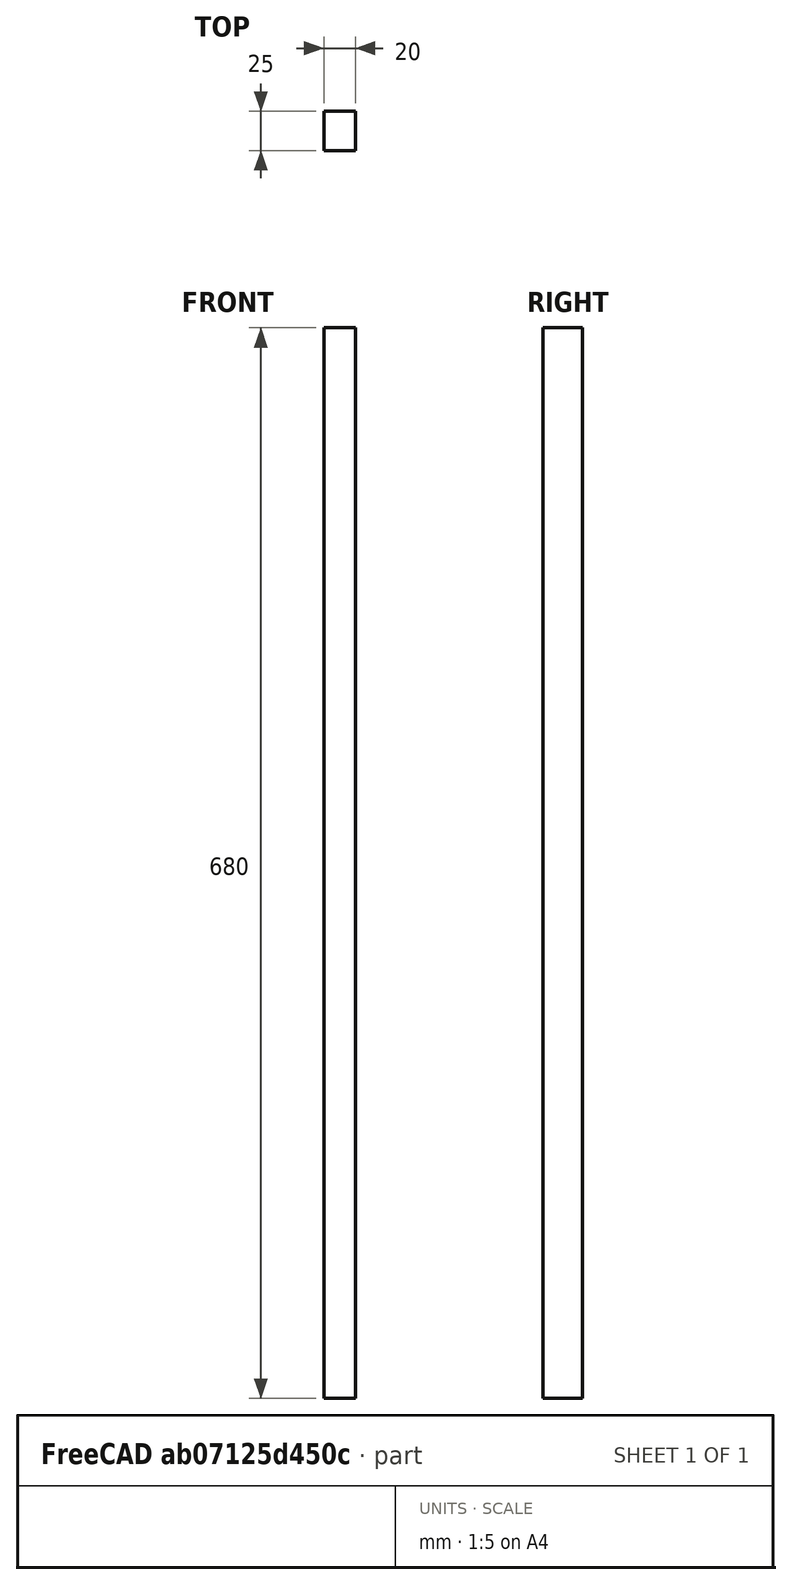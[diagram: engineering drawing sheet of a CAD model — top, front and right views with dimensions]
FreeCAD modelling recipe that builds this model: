
FCSTD DOCUMENT  (FreeCAD 0.21R33771 (Git))
Label: left_bed_rail
License: All rights reserved
LicenseURL: http://en.wikipedia.org/wiki/All_rights_reserved
objects: Sketcher::SketchObject×1, PartDesign::Pad×1, PartDesign::Body×1
note: 4 computed .brp shape members not serialized (recipe doc carries the construction recipe); baked Part::Feature solids carry a one-line shape summary decoded from their .brp

FEATURE [Sketcher::SketchObject] Sketch
  FullyConstrained = true
  MapMode = 5
  Support = -> [XY_Plane]
  sketch-geometry (4):
    g0: LineSegment StartX=-145 StartY=85 StartZ=0 EndX=-125 EndY=85 EndZ=0
    g1: LineSegment StartX=-125 StartY=85 StartZ=0 EndX=-125 EndY=60 EndZ=0
    g2: LineSegment StartX=-125 StartY=60 StartZ=0 EndX=-145 EndY=60 EndZ=0
    g3: LineSegment StartX=-145 StartY=60 StartZ=0 EndX=-145 EndY=85 EndZ=0
  constraints (12):
    c: Coincident(g0,g1)
    c: Coincident(g1,g2)
    c: Coincident(g2,g3)
    c: Coincident(g3,g0)
    c: Horizontal(g0)
    c: Horizontal(g2)
    c: Vertical(g1)
    c: Vertical(g3)
    c: DistanceX(g2,g2) = 20
    c: Distance(g1,g-2) = 125
    c: Distance(g1,g-1) = 60
    c: Distance(g2,g0) = 25
FEATURE [PartDesign::Pad] Pad001
  Direction = (0,0,1)
  Length = 680
  Length2 = 10
  Profile = -> Sketch
  ReferenceAxis = -> Sketch [N_Axis]
  Type = 0
FEATURE [PartDesign::Body] Body  label="bed left rail"
  Group = -> [Sketch,Pad001]
  Origin = -> Origin
  Tip = -> Pad001
